# Revit family: Контейнерный шкаф «Блок композит» Арт 13895
name_source: partatom
category: Антураж
revit_build: Autodesk Revit 2018 (Build: 20180423_1000(x64)
units: mm (PartAtom-declared; Revit-internal decimal feet)

## family parameters
Всегда вертикально = Да
Источник визуального образа = Геометрия семейства
На основе рабочей плоскости = Нет
Общий = Нет
При загрузке вырезать с полостями = Нет
Точка расчета площади = Нет

## types (2) — shared parameters
URL = https://hobbyka.ru
Артикул товара = Арт. 13895
Высота = 1335 мм
Группа модели = Контейнерные площадки для ТБО
Длина = 1600 мм
Изготовитель = ООО «Хоббика»
Изображение типоразмера = Контейнерный шкаф «Блок композит» Арт 13895.jpg
Цвет ТБО = ТБО
Цвет каркаса = Сталь
Цвет отделки = Дерево
Ширина = 924 мм

## per-type parameters (varying)
| type | Версия "Сталь, дерево" | Версия "Сталь, композит" | Материал изделия | Описание |
| Версия "Сталь, дерево" | Да | Нет | Сталь, дерево | Контейнерный шкаф «Блок композит». Версия сталь, дерево |
| Версия "Сталь, композит" | Нет | Да | Сталь, композит | Контейнерный шкаф «Блок композит». Версия сталь, композит |
